# Revit family: RN 81170 Optipress-Aquaplus-KRV-Ventil EA
name_source: partatom
category: Rohrzubehör
units: mm (PartAtom-declared; Revit-internal decimal feet)

## family parameters
Arbeitsebenenbasiert = Nein
Beim Laden mit Abzugskörper schneiden = Nein
Bemaßung runder Anschluss = Durchmesser verwenden
Gemeinsam genutzt = Nein
Immer vertikal = Ja
Teiletyp = Ventil - Zerlegung in

## types (7) — shared parameters
1.010.00.2 Blattnummer der Richtlinie = 17
1.010.00.3 Ausgabedatum (Monat) der Richtlinie = 201601
1.010.00.4 Herstellername = R. Nussbaum AG
1.010.00.5 Revisionsdatum der Datei = 20190528
1.010.00.6 Webadresse des Herstellers = http://www.nussbaum.ch
1.100.00.3 Sortiernummer für Anzeigereihenfolge = 4
1.100.00.4 Produktbezeichnung = Sicherungs- und Ringleitungsarmaturen
1.960/3L.00.8 Link (URL) = https://www.nussbaum.ch
17.700.00.4 Armaturentyp = 6
17.700.00.7 Maximale Betriebstemperatur TB [°C] = 90
17.700.00.8 Maximaler Betriebsdruck (Arbeitsdruck) ps [1.0 · 105 Pa] = 16
Connector Visibility = Nein
EnclosingSpace Visibility = Nein

## per-type parameters (varying)
| type | 1.800.00.3 TGA-Nummer | 1.810.00.3 Hersteller-Bestellnummer | 1.810.00.4 DATANORM-Nummer | 1.810.00.6 GTIN-Nummer | 17.700.00.30 Produktbeschreibung | 17.700.00.5 Nennweite DN | 17.700.00.6 kvs-Wert [m3/h] | CONNECTOR0_DIAMETER_dX_0r | CONNECTOR0_dX_00 | CONNECTOR0_dX_01 | CONNECTOR0_ref_dX | CONNECTOR1_DIAMETER_dX_0r | CONNECTOR1_dX_00 | CONNECTOR1_dX_01 | CONNECTOR1_ref_dX | R. Nussbaum AG 81170.22 de Visibility | R. Nussbaum AG 81170.23 de Visibility | R. Nussbaum AG 81170.24 de Visibility | R. Nussbaum AG 81170.25 de Visibility | R. Nussbaum AG 81170.26 de Visibility | R. Nussbaum AG 81170.27 de Visibility | R. Nussbaum AG 81170.28 de Visibility |
| DN 12 | 0040260000000000000000000000020070000000000000000100000000 | 81170.22 | 81170.22 | 7612945737175 | 81170.22, Optipress-Aquaplus-KRV-Ventil EA, DN=12 | 12 | 5.4 | 12 mm  [stored 0.0393701 ft] | 52 mm | 30 mm | 30 mm | 12 mm  [stored 0.0393701 ft] | 30 mm | 52 mm | 30 mm | Ja | Nein | Nein | Nein | Nein | Nein | Nein |
| DN 15 | 0040260000000000000000000000020070000000000000000200000000 | 81170.23 | 81170.23 | 7612945737182 | 81170.23, Optipress-Aquaplus-KRV-Ventil EA, DN=15 | 15 | 5.4 | 15 mm | 53 mm | 31 mm | 31 mm | 15 mm | 30 mm | 52 mm | 30 mm | Nein | Ja | Nein | Nein | Nein | Nein | Nein |
| DN 20 | 0040260000000000000000000000020070000000000000000300000000 | 81170.24 | 81170.24 | 7612945737489 | 81170.24, Optipress-Aquaplus-KRV-Ventil EA, DN=20 | 20 | 10.8 | 20 mm | 63 mm | 39 mm | 39 mm | 20 mm | 39 mm | 63 mm | 39 mm | Nein | Nein | Ja | Nein | Nein | Nein | Nein |
| DN 25 | 0040260000000000000000000000020070000000000000000400000000 | 81170.25 | 81170.25 | 7612945738134 | 81170.25, Optipress-Aquaplus-KRV-Ventil EA, DN=25 | 25 | 16.8 | 25 mm  [stored 0.082021 ft] | 68 mm | 44 mm | 44 mm | 25 mm  [stored 0.082021 ft] | 44 mm | 68 mm | 44 mm | Nein | Nein | Nein | Ja | Nein | Nein | Nein |
| DN 32 | 0040260000000000000000000000020070000000000000000500000000 | 81170.26 | 81170.26 | 7612945735522 | 81170.26, Optipress-Aquaplus-KRV-Ventil EA, DN=32 | 32 | 31.2 | 32 mm | 78 mm | 52 mm | 52 mm | 32 mm | 51 mm | 77 mm | 51 mm | Nein | Nein | Nein | Nein | Ja | Nein | Nein |
| DN 40 | 0040260000000000000000000000020070000000000000000600000000 | 81170.27 | 81170.27 | 7612945733849 | 81170.27, Optipress-Aquaplus-KRV-Ventil EA, DN=40 | 40 | 45 | 40 mm | 92 mm | 56 mm | 56 mm | 40 mm | 56 mm | 92 mm | 56 mm | Nein | Nein | Nein | Nein | Nein | Ja | Nein |
| DN 50 | 0040260000000000000000000000020070000000000000000700000000 | 81170.28 | 81170.28 | 7612945734112 | 81170.28, Optipress-Aquaplus-KRV-Ventil EA, DN=50 | 50 | 69 | 50 mm | 108 mm | 68 mm | 68 mm | 50 mm | 67 mm | 107 mm | 67 mm | Nein | Nein | Nein | Nein | Nein | Nein | Ja |

note: [stored X ft] marks values corroborated as IEEE doubles in the binary element streams (Revit-internal decimal feet)

## geometry (parser evidence)
native form markers: Sweep x3
no freeform markers — native parametric forms only
